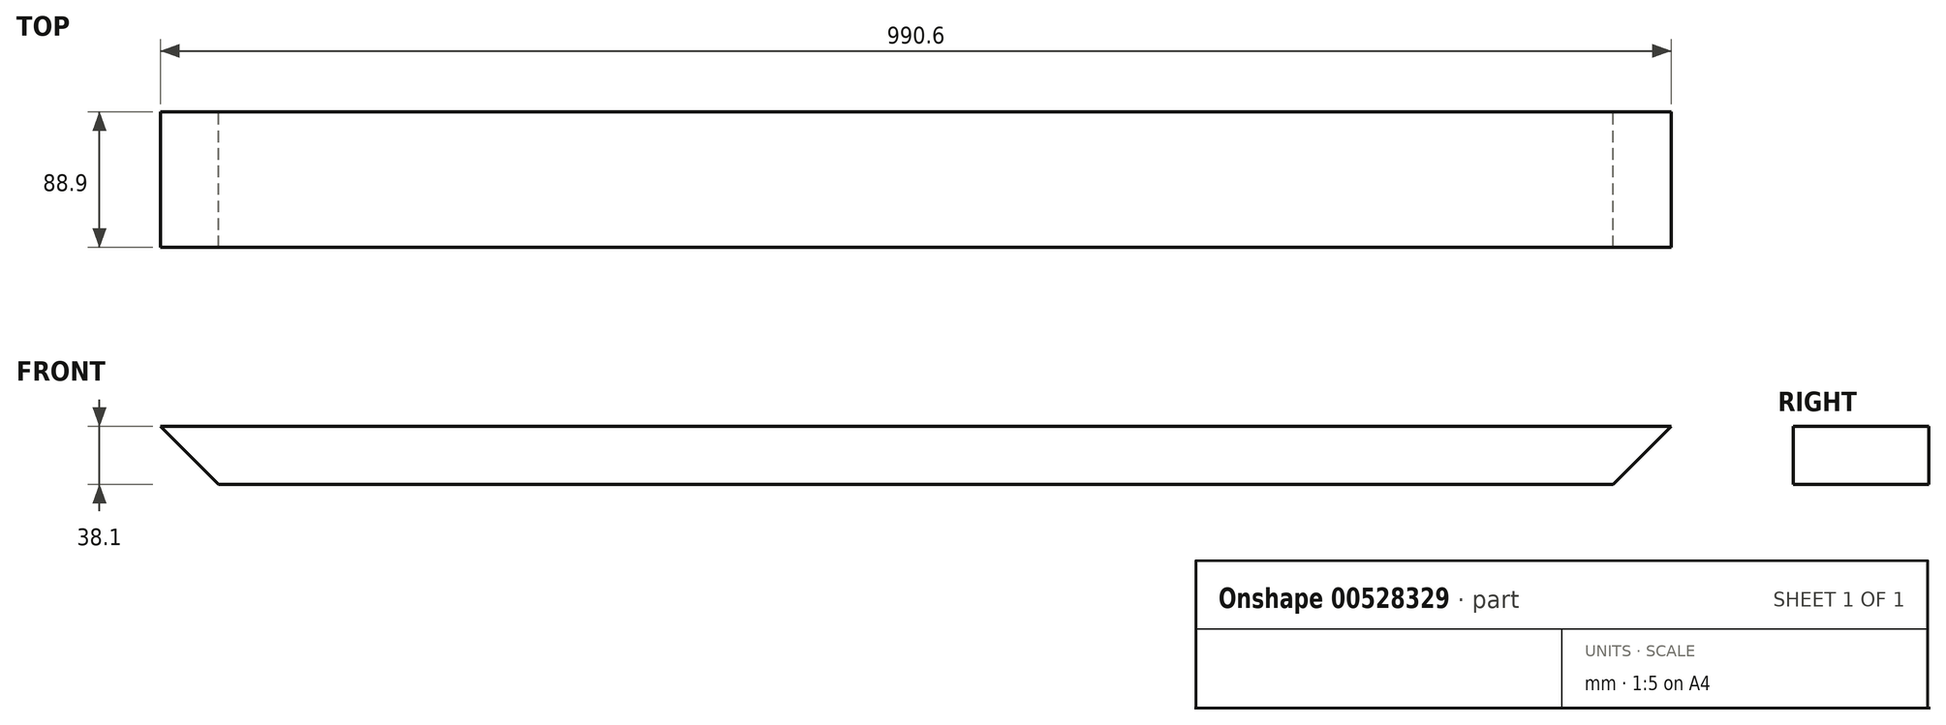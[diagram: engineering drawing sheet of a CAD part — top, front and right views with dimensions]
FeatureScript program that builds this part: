
annotation { "Feature Type Name" : "Feature", "Feature Type Description" : "" }
export const myFeature = defineFeature(function(context is Context, id is Id, definition is map)
    precondition{}
    {
        {
            var Q0;
            Q0=qCreatedBy(makeId("Front.planeOp"),FACE);
            var sketch = newSketch(context, id + "F0", { "sketchPlane" : qUnion([Q0])});
            skLineSegment(sketch, "E0", {"start": v(-990.6, 0) * mm, "end": v(0, 0) * mm});
            skLineSegment(sketch, "E1", {"start": v(-990.6, -1.5) * mm, "end": v(-990.6, 0) * mm, "construction": true});
            skLineSegment(sketch, "E2", {"start": v(0, 0) * mm, "end": v(-38.1, -38.1) * mm});
            skLineSegment(sketch, "E3", {"start": v(-990.6, 0) * mm, "end": v(-952.5, -38.1) * mm});
            skLineSegment(sketch, "E4", {"start": v(-38.1, -38.1) * mm, "end": v(-952.5, -38.1) * mm});
            skLineSegment(sketch, "E5", {"start": v(0, 0) * mm, "end": v(0, -38.1) * mm, "construction": true});
            skSolve(sketch);
        }
        {
            var Q0;
            Q0=makeQuery(id+"F0.imprint","IMPRINT",FACE,{"disambiguationData":[TD([[makeQuery(id+"F0.imprint","IMPRINT",EDGE,{"derivedFrom":sQuery(id+"F0.wireOp",EDGE,"E0")}),-1.0]])]});
            var Q1;
            Q1=sQuery(id+"F0.wireOp",EDGE,"E1");
            extrude(context, id + "F1", {"entities" : qUnion([Q0]), "surfaceEntities" : qUnion([Q1]), "depth" : 88.9 * mm, "offsetDistance" : 25 * mm});
        }
    });
